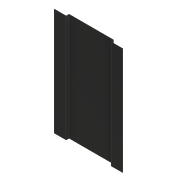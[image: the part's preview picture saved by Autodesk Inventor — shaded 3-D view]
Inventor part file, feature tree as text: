
AUTODESK INVENTOR PART (.ipt)
format: ipt  version: 2018 (Build 220112000, 112)  size: 114,688 bytes
history: native  units: mm
features: sheet_metal_op x3, sketch x1, other x1
ambient origin geometry x8: Origin, YZ Plane, XZ Plane, XY Plane, X Axis, Y Axis, Z Axis, Center Point
bodies: Solid1 (feature_tree)
feature tree (5):
  sheet_metal_op  "Contour Flange1"
  sketch  "Sketch1"  dims[d3=90.0deg d4=90.0deg d6=350.0mm d7=15.0mm d8=1.0mm d9=1.0mm d10=0.5mm d11=2.0mm d12=1.0mm d13=550.0mm d14=1.0mm d15=1.0mm d16=4.0mm d17=1.0mm d18=1.0mm d19=60.0mm]
  other  "Plate1"
  sheet_metal_op  "Bend1"
  sheet_metal_op  "Corner1"
